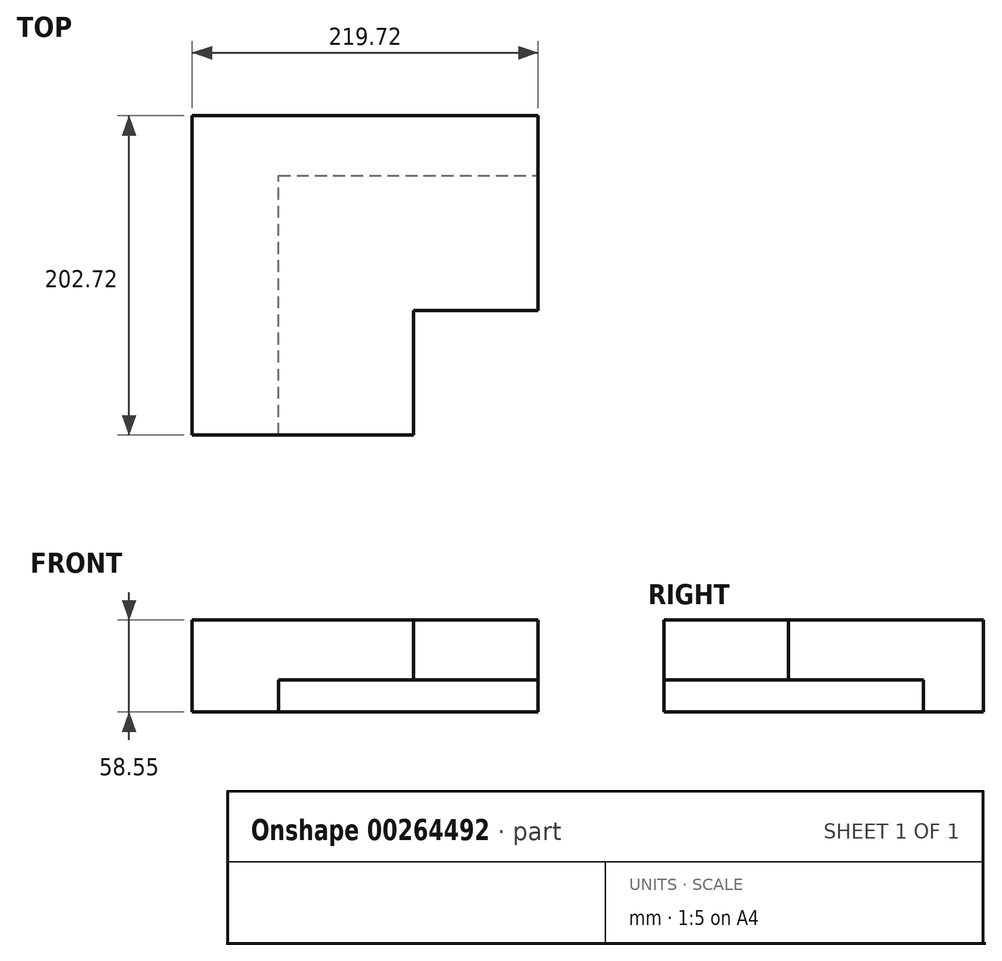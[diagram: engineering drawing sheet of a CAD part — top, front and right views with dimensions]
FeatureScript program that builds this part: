
annotation { "Feature Type Name" : "Feature", "Feature Type Description" : "" }
export const myFeature = defineFeature(function(context is Context, id is Id, definition is map)
    precondition{}
    {
        {
            var Q0;
            Q0=qCreatedBy(makeId("Top.planeOp"),FACE);
            var sketch = newSketch(context, id + "F0", { "sketchPlane" : qUnion([Q0])});
            skLineSegment(sketch, "E0", {"start": v(107.86, 53.86) * mm, "end": v(107.86, 107.86) * mm});
            skLineSegment(sketch, "E1", {"start": v(107.86, 107.86) * mm, "end": v(-107.86, 107.86) * mm});
            skLineSegment(sketch, "E2", {"start": v(-107.86, 107.86) * mm, "end": v(-107.86, -107.86) * mm});
            skLineSegment(sketch, "E3", {"start": v(-107.86, -107.86) * mm, "end": v(-53.86, -107.86) * mm});
            skLineSegment(sketch, "E4", {"start": v(-53.86, -107.86) * mm, "end": v(-53.86, 53.86) * mm});
            skLineSegment(sketch, "E5", {"start": v(-53.86, 53.86) * mm, "end": v(107.86, 53.86) * mm});
            skLineSegment(sketch, "E6", {"start": v(0, 107.86) * mm, "end": v(0, 0) * mm, "construction": true});
            skLineSegment(sketch, "E7", {"start": v(0, 0) * mm, "end": v(-107.86, 0) * mm, "construction": true});
            skSolve(sketch);
        }
        {
            var Q0;
            Q0=makeQuery(id+"F0.imprint","IMPRINT",FACE,{"disambiguationData":[TD([[makeQuery(id+"F0.imprint","IMPRINT",EDGE,{"derivedFrom":sQuery(id+"F0.wireOp",EDGE,"E0")}),1.0]])]});
            extrude(context, id + "F1", {"entities" : qUnion([Q0]), "depth" : 20.55 * mm});
        }
        {
            var Q0;
            Q0=makeQuery(id+"F1.opExtrude","CAP_FACE",FACE,{"disambiguationData":[OSD([sQuery(id+"F0.wireOp",EDGE,"E0"),sQuery(id+"F0.wireOp",EDGE,"E1"),sQuery(id+"F0.wireOp",EDGE,"E2"),sQuery(id+"F0.wireOp",EDGE,"E3"),sQuery(id+"F0.wireOp",EDGE,"E4"),sQuery(id+"F0.wireOp",EDGE,"E5")])],"isStart":false});
            var sketch = newSketch(context, id + "F2", { "sketchPlane" : qUnion([Q0])});
            skLineSegment(sketch, "E8.bottom", {"start": v(-107.86, 107.86) * mm, "end": v(107.86, 107.86) * mm});
            skLineSegment(sketch, "E8.top", {"start": v(-107.86, -107.86) * mm, "end": v(107.86, -107.86) * mm});
            skLineSegment(sketch, "E8.left", {"start": v(-107.86, 107.86) * mm, "end": v(-107.86, -107.86) * mm});
            skLineSegment(sketch, "E8.right", {"start": v(107.86, 107.86) * mm, "end": v(107.86, -107.86) * mm});
            skSolve(sketch);
        }
        {
            var Q0;
            Q0 = qSketchRegion(id + "F2", true);
            extrude(context, id + "F3", {"entities" : qUnion([Q0]), "operationType" : NewBodyOperationType.ADD, "depth" : 38 * mm});
        }
        {
            var Q0;
            Q0=makeQuery(id+"F3.opExtrude","CAP_FACE",FACE,{"disambiguationData":[OSD([sQuery(id+"F2.wireOp",EDGE,"E8.bottom"),sQuery(id+"F2.wireOp",EDGE,"E8.top"),sQuery(id+"F2.wireOp",EDGE,"E8.left"),sQuery(id+"F2.wireOp",EDGE,"E8.right")])],"isStart":false});
            var sketch = newSketch(context, id + "F4", { "sketchPlane" : qUnion([Q0])});
            skLineSegment(sketch, "E9", {"start": v(-107.86, -107.86) * mm, "end": v(-110.86, -107.86) * mm});
            skLineSegment(sketch, "E10", {"start": v(-110.86, -107.86) * mm, "end": v(-110.86, 110.86) * mm});
            skLineSegment(sketch, "E11", {"start": v(-110.86, 110.86) * mm, "end": v(107.86, 110.86) * mm});
            skLineSegment(sketch, "E12", {"start": v(107.86, 110.86) * mm, "end": v(107.86, 107.86) * mm});
            skLineSegment(sketch, "E13", {"start": v(107.86, 107.86) * mm, "end": v(-107.86, 107.86) * mm});
            skLineSegment(sketch, "E14", {"start": v(-107.86, 107.86) * mm, "end": v(-107.86, -107.86) * mm});
            skSolve(sketch);
        }
        {
            var Q0;
            Q0 = qSketchRegion(id + "F4", true);
            var Q1;
            Q1=makeQuery(id+"F1.opExtrude","CAP_FACE",FACE,{"disambiguationData":[OSD([sQuery(id+"F0.wireOp",EDGE,"E0"),sQuery(id+"F0.wireOp",EDGE,"E1"),sQuery(id+"F0.wireOp",EDGE,"E2"),sQuery(id+"F0.wireOp",EDGE,"E3"),sQuery(id+"F0.wireOp",EDGE,"E4"),sQuery(id+"F0.wireOp",EDGE,"E5")])],"isStart":true});
            extrude(context, id + "F5", {"entities" : qUnion([Q0]), "operationType" : NewBodyOperationType.ADD, "endBound" : BoundingType.UP_TO_SURFACE, "oppositeDirection" : true, "endBoundEntityFace" : qUnion([Q1]), "depth" : 25 * mm});
        }
        {
            var Q0;
            Q0=makeQuery(id+"F3.opExtrude","CAP_FACE",FACE,{"disambiguationData":[OSD([sQuery(id+"F2.wireOp",EDGE,"E8.bottom"),sQuery(id+"F2.wireOp",EDGE,"E8.top"),sQuery(id+"F2.wireOp",EDGE,"E8.left"),sQuery(id+"F2.wireOp",EDGE,"E8.right")])],"isStart":true});
            var sketch = newSketch(context, id + "F6", { "sketchPlane" : qUnion([Q0])});
            skLineSegment(sketch, "E15.bottom", {"start": v(31.86, 107.86) * mm, "end": v(107.86, 107.86) * mm});
            skLineSegment(sketch, "E15.top", {"start": v(31.86, 31.86) * mm, "end": v(107.86, 31.86) * mm});
            skLineSegment(sketch, "E15.left", {"start": v(31.86, 107.86) * mm, "end": v(31.86, 31.86) * mm});
            skLineSegment(sketch, "E15.right", {"start": v(107.86, 107.86) * mm, "end": v(107.86, 31.86) * mm});
            skSolve(sketch);
        }
        {
            var Q0;
            Q0 = qSketchRegion(id + "F6", true);
            extrude(context, id + "F7", {"entities" : qUnion([Q0]), "operationType" : NewBodyOperationType.REMOVE, "endBound" : BoundingType.THROUGH_ALL, "oppositeDirection" : true, "depth" : 25 * mm});
        }
        {
            var Q0;
            Q0=makeQuery(id+"F5.boolean.opBoolean","MERGE",FACE,{"derivedFrom":[makeQuery(id+"F3.boolean.opBoolean","MERGE",FACE,{"derivedFrom":[makeQuery(id+"F1.opExtrude","SWEPT_FACE",FACE,{"disambiguationData":[OSD([sQuery(id+"F0.wireOp",EDGE,"E0")])]}),makeQuery(id+"F3.opExtrude","SWEPT_FACE",FACE,{"disambiguationData":[OSD([sQuery(id+"F2.wireOp",EDGE,"E8.right")])]})]}),makeQuery(id+"F5.opExtrude","SWEPT_FACE",FACE,{"disambiguationData":[OSD([sQuery(id+"F4.wireOp",EDGE,"E12")])]})]});
            var sketch = newSketch(context, id + "F8", { "sketchPlane" : qUnion([Q0])});
            skLineSegment(sketch, "E16", {"start": v(-31.86, 58.55) * mm, "end": v(-31.86, 20.55) * mm});
            skLineSegment(sketch, "E17", {"start": v(-31.86, 20.55) * mm, "end": v(53.86, 20.55) * mm});
            skLineSegment(sketch, "E18", {"start": v(53.86, 20.55) * mm, "end": v(53.86, 0) * mm});
            skLineSegment(sketch, "E19", {"start": v(53.86, 0) * mm, "end": v(110.86, 0) * mm});
            skLineSegment(sketch, "E20", {"start": v(110.86, 0) * mm, "end": v(110.86, 58.55) * mm});
            skLineSegment(sketch, "E21", {"start": v(110.86, 58.55) * mm, "end": v(-31.86, 58.55) * mm});
            skSolve(sketch);
        }
        {
            var Q0;
            Q0 = qSketchRegion(id + "F8", true);
            extrude(context, id + "F9", {"entities" : qUnion([Q0]), "operationType" : NewBodyOperationType.ADD, "depth" : 3 * mm});
        }
        {
            var Q0;
            Q0=makeQuery(id+"F5.boolean.opBoolean","MERGE",FACE,{"derivedFrom":[makeQuery(id+"F3.boolean.opBoolean","MERGE",FACE,{"derivedFrom":[makeQuery(id+"F1.opExtrude","SWEPT_FACE",FACE,{"disambiguationData":[OSD([sQuery(id+"F0.wireOp",EDGE,"E3")])]}),makeQuery(id+"F3.opExtrude","SWEPT_FACE",FACE,{"disambiguationData":[OSD([sQuery(id+"F2.wireOp",EDGE,"E8.top")])]})]}),makeQuery(id+"F5.opExtrude","SWEPT_FACE",FACE,{"disambiguationData":[OSD([sQuery(id+"F4.wireOp",EDGE,"E9")])]})]});
            var sketch = newSketch(context, id + "F10", { "sketchPlane" : qUnion([Q0])});
            skLineSegment(sketch, "E22", {"start": v(-110.86, 58.55) * mm, "end": v(-110.86, 0) * mm});
            skLineSegment(sketch, "E23", {"start": v(-110.86, 0) * mm, "end": v(-53.86, 0) * mm});
            skLineSegment(sketch, "E24", {"start": v(-53.86, 0) * mm, "end": v(-53.86, 20.55) * mm});
            skLineSegment(sketch, "E25", {"start": v(-53.86, 20.55) * mm, "end": v(31.86, 20.55) * mm});
            skLineSegment(sketch, "E26", {"start": v(31.86, 20.55) * mm, "end": v(31.86, 58.55) * mm});
            skLineSegment(sketch, "E27", {"start": v(31.86, 58.55) * mm, "end": v(-110.86, 58.55) * mm});
            skSolve(sketch);
        }
        {
            var Q0;
            Q0 = qSketchRegion(id + "F10", true);
            extrude(context, id + "F11", {"entities" : qUnion([Q0]), "operationType" : NewBodyOperationType.ADD, "depth" : 3 * mm});
        }
        {
            var Q0;
            {var subQ0=sQuery(id+"F0.wireOp",EDGE,"E5");var subQ1=sQuery(id+"F0.wireOp",EDGE,"E4");var subQ2=sQuery(id+"F0.wireOp",EDGE,"E3");var subQ3=sQuery(id+"F0.wireOp",EDGE,"E2");var subQ4=sQuery(id+"F0.wireOp",EDGE,"E1");var subQ5=sQuery(id+"F0.wireOp",EDGE,"E0");Q0=makeQuery(id+"F11.boolean.opBoolean","MERGE",FACE,{"derivedFrom":[makeQuery(id+"F9.boolean.opBoolean","MERGE",FACE,{"derivedFrom":[makeQuery(id+"F5.boolean.opBoolean","MERGE",FACE,{"derivedFrom":[makeQuery(id+"F1.opExtrude","CAP_FACE",FACE,{"disambiguationData":[OSD([subQ5,subQ4,subQ3,subQ2,subQ1,subQ0])],"isStart":true}),makeQuery(id+"F5.opExtrude","CAP_FACE",FACE,{"disambiguationData":[OSD([subQ5,subQ4,subQ3,subQ2,subQ1,subQ0])],"isStart":false})]}),makeQuery(id+"F9.opExtrude","SWEPT_FACE",FACE,{"disambiguationData":[OSD([sQuery(id+"F8.wireOp",EDGE,"E19")])]})]}),makeQuery(id+"F11.opExtrude","SWEPT_FACE",FACE,{"disambiguationData":[OSD([sQuery(id+"F10.wireOp",EDGE,"E23")])]})]});}
            var sketch = newSketch(context, id + "F12", { "sketchPlane" : qUnion([Q0])});
            skLineSegment(sketch, "E28.bottom", {"start": v(-110.86, -110.86) * mm, "end": v(110.86, -110.86) * mm});
            skLineSegment(sketch, "E28.top", {"start": v(-110.86, -91.86) * mm, "end": v(110.86, -91.86) * mm});
            skLineSegment(sketch, "E28.left", {"start": v(-110.86, -110.86) * mm, "end": v(-110.86, -91.86) * mm});
            skLineSegment(sketch, "E28.right", {"start": v(110.86, -110.86) * mm, "end": v(110.86, -91.86) * mm});
            skSolve(sketch);
        }
        {
            var Q0;
            Q0 = qSketchRegion(id + "F12", true);
            extrude(context, id + "F13", {"entities" : qUnion([Q0]), "operationType" : NewBodyOperationType.REMOVE, "endBound" : BoundingType.THROUGH_ALL, "oppositeDirection" : true, "depth" : 25 * mm});
        }
        {
            var Q0;
            {var subQ0=sQuery(id+"F0.wireOp",EDGE,"E5");var subQ1=sQuery(id+"F0.wireOp",EDGE,"E4");var subQ2=sQuery(id+"F0.wireOp",EDGE,"E3");var subQ3=sQuery(id+"F0.wireOp",EDGE,"E2");var subQ4=sQuery(id+"F0.wireOp",EDGE,"E1");var subQ5=sQuery(id+"F0.wireOp",EDGE,"E0");Q0=makeQuery(id+"F11.boolean.opBoolean","MERGE",FACE,{"derivedFrom":[makeQuery(id+"F9.boolean.opBoolean","MERGE",FACE,{"derivedFrom":[makeQuery(id+"F5.boolean.opBoolean","MERGE",FACE,{"derivedFrom":[makeQuery(id+"F1.opExtrude","CAP_FACE",FACE,{"disambiguationData":[OSD([subQ5,subQ4,subQ3,subQ2,subQ1,subQ0])],"isStart":true}),makeQuery(id+"F5.opExtrude","CAP_FACE",FACE,{"disambiguationData":[OSD([subQ5,subQ4,subQ3,subQ2,subQ1,subQ0])],"isStart":false})]}),makeQuery(id+"F9.opExtrude","SWEPT_FACE",FACE,{"disambiguationData":[OSD([sQuery(id+"F8.wireOp",EDGE,"E19")])]})]}),makeQuery(id+"F11.opExtrude","SWEPT_FACE",FACE,{"disambiguationData":[OSD([sQuery(id+"F10.wireOp",EDGE,"E23")])]})]});}
            var sketch = newSketch(context, id + "F14", { "sketchPlane" : qUnion([Q0])});
            skLineSegment(sketch, "E29.bottom", {"start": v(-110.86, 110.86) * mm, "end": v(-108.86, 110.86) * mm});
            skLineSegment(sketch, "E29.top", {"start": v(-110.86, -91.86) * mm, "end": v(-108.86, -91.86) * mm});
            skLineSegment(sketch, "E29.left", {"start": v(-110.86, 110.86) * mm, "end": v(-110.86, -91.86) * mm});
            skLineSegment(sketch, "E29.right", {"start": v(-108.86, 110.86) * mm, "end": v(-108.86, -91.86) * mm});
            skSolve(sketch);
        }
        {
            var Q0;
            Q0 = qSketchRegion(id + "F14", true);
            extrude(context, id + "F15", {"entities" : qUnion([Q0]), "operationType" : NewBodyOperationType.REMOVE, "endBound" : BoundingType.THROUGH_ALL, "oppositeDirection" : true, "depth" : 25 * mm});
        }
    });
